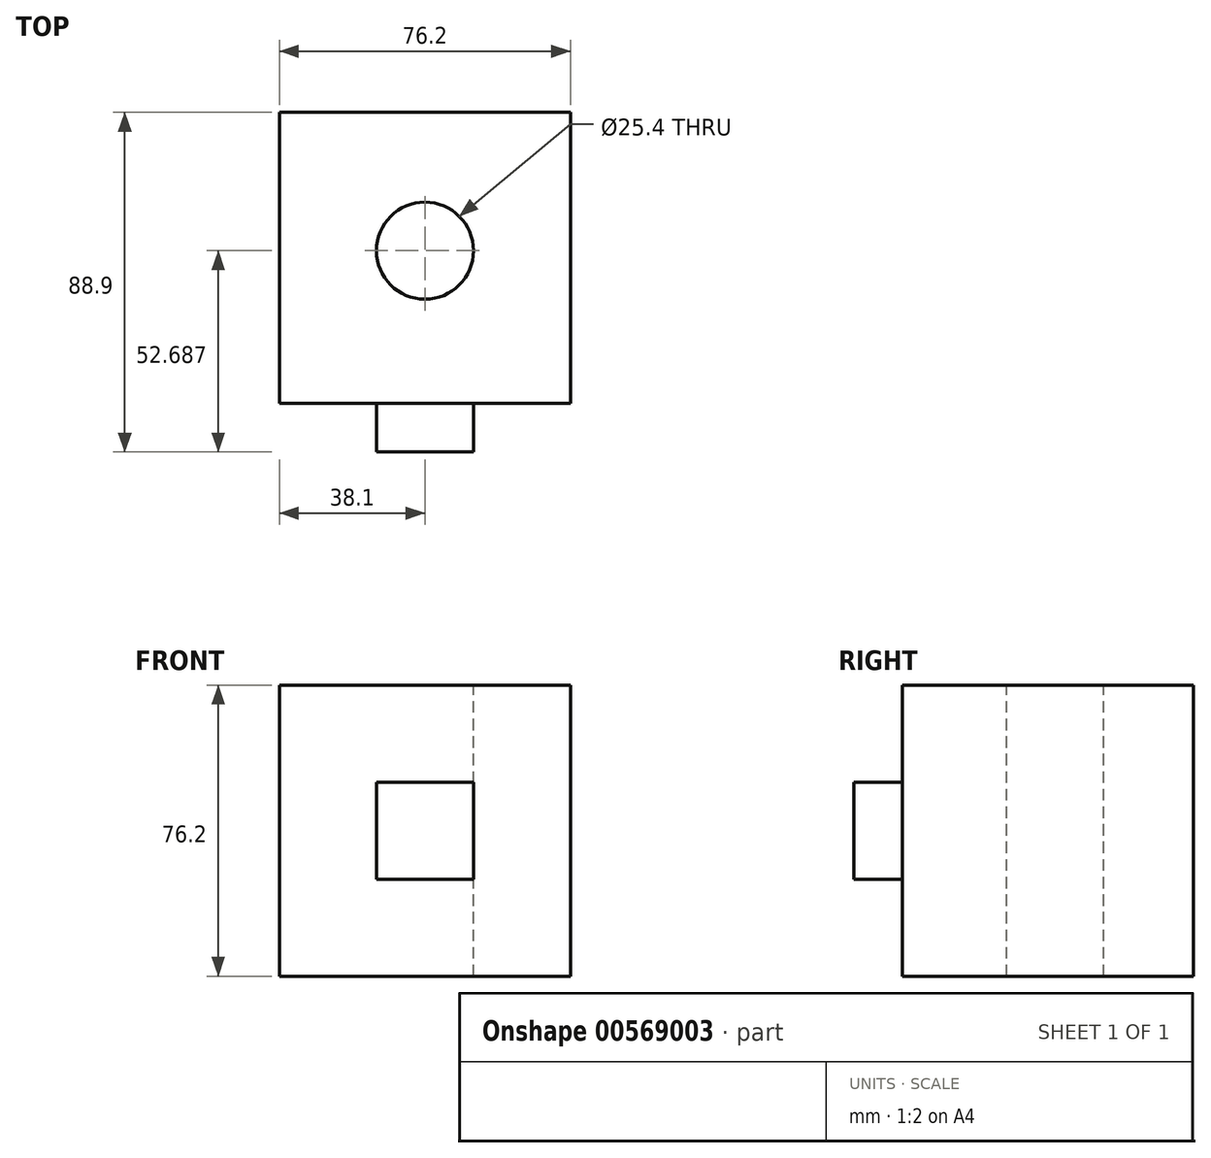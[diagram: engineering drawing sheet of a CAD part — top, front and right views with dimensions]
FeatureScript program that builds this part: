
annotation { "Feature Type Name" : "Feature", "Feature Type Description" : "" }
export const myFeature = defineFeature(function(context is Context, id is Id, definition is map)
    precondition{}
    {
        {
            var Q0;
            Q0=qCreatedBy(makeId("Front.planeOp"),FACE);
            var sketch = newSketch(context, id + "F0", { "sketchPlane" : qUnion([Q0])});
            skLineSegment(sketch, "E0.bottom", {"start": v(0, 0) * mm, "end": v(76.2, 0) * mm});
            skLineSegment(sketch, "E0.top", {"start": v(0, 76.2) * mm, "end": v(76.2, 76.2) * mm});
            skLineSegment(sketch, "E0.left", {"start": v(0, 0) * mm, "end": v(0, 76.2) * mm});
            skLineSegment(sketch, "E0.right", {"start": v(76.2, 0) * mm, "end": v(76.2, 76.2) * mm});
            skSolve(sketch);
        }
        {
            var Q0;
            Q0=makeQuery(id+"F0.imprint","IMPRINT",FACE,{"disambiguationData":[TD([[makeQuery(id+"F0.imprint","IMPRINT",EDGE,{"derivedFrom":sQuery(id+"F0.wireOp",EDGE,"E0.bottom")}),1.0]])]});
            extrude(context, id + "F1", {"entities" : qUnion([Q0]), "depth" : 76.2 * mm, "offsetDistance" : 25.4 * mm});
        }
        {
            var Q0;
            Q0=makeQuery(id+"F1.opExtrude","SWEPT_FACE",FACE,{"disambiguationData":[OSD([sQuery(id+"F0.wireOp",EDGE,"E0.top")])]});
            var sketch = newSketch(context, id + "F2", { "sketchPlane" : qUnion([Q0])});
            skPoint(sketch, "E1", {"position": v(38.1, -36.21) * mm});
            skSolve(sketch);
        }
        {
            var Q0;
            Q0=sQuery(id+"F2.wireOp",VERTEX,"E1");
            var Q1;
            Q1=makeQuery(id+"F1.opExtrude","SWEPT_BODY",BODY,{"disambiguationData":[OSD([sQuery(id+"F0.wireOp",EDGE,"E0.bottom"),sQuery(id+"F0.wireOp",EDGE,"E0.top"),sQuery(id+"F0.wireOp",EDGE,"E0.left"),sQuery(id+"F0.wireOp",EDGE,"E0.right")])]});
            hole(context, id + "F3", {"style" : HoleStyle.SIMPLE, "endStyle" : HoleEndStyle.THROUGH, "holeDiameter" : 25.4 * mm, "isTappedThrough" : true, "tappedDepth" : 12.7 * mm, "tapClearance" : 3, "locations" : qUnion([Q0]), "scope" : qUnion([Q1])});
        }
        {
            var Q0;
            Q0=makeQuery(id+"F1.opExtrude","CAP_FACE",FACE,{"disambiguationData":[OSD([sQuery(id+"F0.wireOp",EDGE,"E0.bottom"),sQuery(id+"F0.wireOp",EDGE,"E0.top"),sQuery(id+"F0.wireOp",EDGE,"E0.left"),sQuery(id+"F0.wireOp",EDGE,"E0.right")])],"isStart":false});
            var sketch = newSketch(context, id + "F4", { "sketchPlane" : qUnion([Q0])});
            skLineSegment(sketch, "E2.bottom", {"start": v(25.4, 25.4) * mm, "end": v(50.8, 25.4) * mm});
            skLineSegment(sketch, "E2.top", {"start": v(25.4, 50.8) * mm, "end": v(50.8, 50.8) * mm});
            skLineSegment(sketch, "E2.left", {"start": v(25.4, 25.4) * mm, "end": v(25.4, 50.8) * mm});
            skLineSegment(sketch, "E2.right", {"start": v(50.8, 25.4) * mm, "end": v(50.8, 50.8) * mm});
            skSolve(sketch);
        }
        {
            var Q0;
            Q0 = qSketchRegion(id + "F4", true);
            extrude(context, id + "F5", {"entities" : qUnion([Q0]), "operationType" : NewBodyOperationType.ADD, "depth" : 12.7 * mm, "offsetDistance" : 25.4 * mm});
        }
    });
